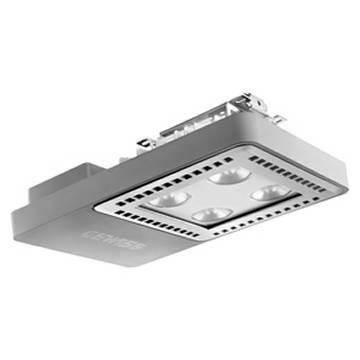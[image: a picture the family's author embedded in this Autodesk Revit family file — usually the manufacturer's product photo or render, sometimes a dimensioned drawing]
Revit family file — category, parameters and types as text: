
# Revit family: Lighting-Industrial-GEWISS-SMART[4]HE_HIGHBAYS-LED_1M
name_source: partatom
category: Apparecchi per illuminazione
units: mm (PartAtom-declared; Revit-internal decimal feet)

## family parameters
Basato su piano di lavoro = Sì
Condiviso = No
Numero OmniClass = 23.80.00.00
Punto di calcolo locali = Sì
Quota connettore circolare = Usa diametro
Sempre verticale = No
Sorgente d'illuminazione = No
Taglio con vuoti quando caricato = No
Tipo di parte = Normale
Titolo OmniClass = Electric Power and Lighting

## types (36) — shared parameters
Application = Internal
Body = PA6 "Halogen Free" loaded fibreglass
Carico apparente = 50 VA
Catalogue = LIGHTING
Classification: = -
Classificazione = Lighting
Color Rendering Index = CRI-80
Colour = Grey RAL 7035
Colour : = Grey RAL 7035
Commenti sul wattaggio = 50W
Context = Logistics and industrial manufacturing lighting
Control System = ON / OFF
Control System : = ON / OFF
DIN 18032-3 certification = With Bracket - Rope Kit + terminal&nbsp;(in approval)
Device with reduced surface temperature = Yes
Distanza tot_plafoniera = 74 mm  [stored 0.242782 ft]
Driver = Included
Driver Box = Built-in
Electrocod = 2444
Eletrical and lighting features = -
External screw = Stainless steel
Fixing = -
Gasket = anti-aging silicone
General information = -
Glow Wire Test : = 850 °C
IDF = caca2710-84d7-41a6-9312-c1c8a4914de0
IDT = 33be10311be341e0b261e3e80f29047b
IP degree = IP66
IPEA = -
Immagine tipo = GWL1071.jpg
Installationa and maintenance = -
Insulation class = I
LED Maintenance = Non-replaceable
Lampada = LED
Larghezza = 253 mm  [stored 0.830052 ft]
Lifetime = L90B10 (Tq+25°C) = 70.000 h - L90B10 (Tq+50°C) = 35.000 h
Locking Hook = -
Luminaire = LED Industrial ReflectorÂ
Lunghezza = 383 mm  [stored 1.25656 ft]
Materials = -
Maximum surface exposed to the wind : = 0,097 m²
Motore = <Per categoria>
Mouting and installation = Ceiling - Wallmounting - Suspension
Operating temperature : = -30°C ÷ +50 °C
Optic Maintenance = Non-replaceable
Optic and illuminating features = -
Overvoltage protection = DM 6kV / CM 6kV
Photobiological Risk Class = RG0
Plafoniera = <Per categoria>
Produttore = GEWISS S.p.A.
Prospetto di default = 1219 mm
Raggio led = 30 mm  [stored 0.0984252 ft]
Rated frequency (Hz) = 50/60 Hz
Shield type = Tempered glass Thickness 4mm
Shock resistance = IK08
Spessore plafoniera = 40 mm  [stored 0.131234 ft]
Standard Deviation Colour Matching = SDCM = 3
Standard- = EN 60598-1 ; EN 60598-2-1 ; EN 60598-2-24
Standards and approvals = -
Stocking temperature = -40 +70 °C
Supply voltage = 220 - 240 V
System power = 48W
Technical sheet = https://www.gewiss.com
Tilt- = With bracket accessory
Trasformatore = <Per categoria>
Type of light source = LED - Not replaceable
URL = https://www.gewiss.com
Unique digital code (Datamatrix) = Datamatrix
Version file RFA = 20.11
Vetro acceso = Lampada accesa
Voltaggio = 230 V
Warranty = 5 years
Weight (kg): = 3,5
Wiring = With GW connect watertight connector

## per-type parameters (varying)
| type | Colour temperature | Descrizione | Efficiency (lm/W) | Lumen output (lm) | Modello | Optic | Optic : | SEO | Unified Glare Rating |
| GWS4120AP857 - SMART4LB 1M ST.AL.ON/OFF 90° 57K | 5700K | SMART[4]LB 1M ST.AL.ON/OFF 90° 57K | 150 | 7200 | GWS4120AP857 | 90° | Metallic PC reflector and PMMA lenses |  | UGR - 25 |
| GWS4122AC830 - SMART4LB 1M C.PAS.ON/OFF ASI.30K | 3000K | SMART[4]LB 1M C.PAS.ON/OFF ASI.30K | 125 | 6000 | GWS4122AC830 | Asymmetrical | Metallic PC reflector and PMMA lenses | Low bay | - |
| GWS4120AQ857 - SMART4LB 1M ST.AL.ON/OFF ELL.57K | 5700K | SMART[4]LB 1M ST.AL.ON/OFF ELL.57K | 131 | 6300 | GWS4120AQ857 | Elliptical | Metallic PC reflector and PMMA lenses | Low bay | - |
| GWS4122AF830 - SMART4LB 1M C.PAS.ON/OFF 30° 30K | 3000K | SMART[4]LB 1M C.PAS.ON/OFF 30° 30K | 138 | 6600 | GWS4122AF830 | 30° | Metallic PC reflector and PMMA lenses |  | UGR - 22 |
| GWS4120AQ830 - SMART4LB 1M ST.AL.ON/OFF ELL.30K | 3000K | SMART[4]LB 1M ST.AL.ON/OFF ELL.30K | 125 | 6000 | GWS4120AQ830 | Elliptical | Metallic PC reflector and PMMA lenses | Low bay | - |
| GWS4122AQ840 - SMART4LB 1M C.PAS.ON/OFF ELL.40K | 4000K | SMART[4]LB 1M C.PAS.ON/OFF ELL.40K | 131 | 6300 | GWS4122AQ840 | Elliptical | Metallic PC reflector and PMMA lenses | Low bay | - |
| GWS4122AH857 - SMART4LB 1M C.PAS.ON/OFF 60° 57K | 5700K | SMART[4]LB 1M C.PAS.ON/OFF 60° 57K | 146 | 7000 | GWS4122AH857 | 60° | Metallic PC reflector and PMMA lenses |  | UGR - 22 |
| GWS4120AF830 - SMART4LB 1M ST.AL.ON/OFF 30° 30K | 3000K | SMART[4]LB 1M ST.AL.ON/OFF 30° 30K | 138 | 6600 | GWS4120AF830 | 30° | Metallic PC reflector and PMMA lenses |  | UGR - 22 |
| GWS4122AC857 - SMART4LB 1M C.PAS.ON/OFF ASI.57K | 5700K | SMART[4]LB 1M C.PAS.ON/OFF ASI.57K | 131 | 6300 | GWS4122AC857 | Asymmetrical | Metallic PC reflector and PMMA lenses | Low bay | - |
| GWS4120AH840 - SMART4LB 1M ST.AL.ON/OFF 60° 40K | 4000K | SMART[4]LB 1M ST.AL.ON/OFF 60° 40K | 146 | 7000 | GWS4120AH840 | 60° | Metallic PC reflector and PMMA lenses |  | UGR - 22 |
| GWS4122AP840 - SMART4LB 1M C.PAS.ON/OFF 90° 40K | 4000K | SMART[4]LB 1M C.PAS.ON/OFF 90° 40K | 150 | 7200 | GWS4122AP840 | 90° | Metallic PC reflector and PMMA lenses |  | UGR - 25 |
| GWS4120AH857 - SMART4LB 1M ST.AL.ON/OFF 60° 57K | 5700K | SMART[4]LB 1M ST.AL.ON/OFF 60° 57K | 146 | 7000 | GWS4120AH857 | 60° | Metallic PC reflector and PMMA lenses |  | UGR - 22 |
| GWS4122AP857 - SMART4LB 1M C.PAS.ON/OFF 90° 57K | 5700K | SMART[4]LB 1M C.PAS.ON/OFF 90° 57K | 150 | 7200 | GWS4122AP857 | 90° | Metallic PC reflector and PMMA lenses |  | UGR - 25 |
| GWS4120AA840 - SMART4LB 1M ST.AL.ON/OFF ARR.40K | 4000K | SMART[4]LB 1M ST.AL.ON/OFF ARR.40K | 148 | 7100 | GWS4120AA840 | Array | Metallized polycarbonate reflector |  | - |
| GWS4120AP830 - SMART4LB 1M ST.AL.ON/OFF 90° 30K | 3000K | SMART[4]LB 1M ST.AL.ON/OFF 90° 30K | 142 | 6800 | GWS4120AP830 | 90° | Metallic PC reflector and PMMA lenses |  | UGR - 25 |
| GWS4120AA830 - SMART4LB 1M ST.AL.ON/OFF ARR.30K | 3000K | SMART[4]LB 1M ST.AL.ON/OFF ARR.30K | 140 | 6700 | GWS4120AA830 | Array | Metallized polycarbonate reflector |  | - |
| GWS4122AA857 - SMART4LB 1M C.PAS.ON/OFF ARR.57K | 5700K | SMART[4]LB 1M C.PAS.ON/OFF ARR.57K | 148 | 7100 | GWS4122AA857 | Array | Metallized polycarbonate reflector |  | - |
| GWS4122AC840 - SMART4LB 1M C.PAS.ON/OFF ASI.40K | 4000K | SMART[4]LB 1M C.PAS.ON/OFF ASI.40K | 131 | 6300 | GWS4122AC840 | Asymmetrical | Metallic PC reflector and PMMA lenses | Low bay | - |
| GWS4120AH830 - SMART4LB 1M ST.AL.ON/OFF 60° 30K | 3000K | SMART[4]LB 1M ST.AL.ON/OFF 60° 30K | 140 | 6700 | GWS4120AH830 | 60° | Metallic PC reflector and PMMA lenses |  | UGR - 22 |
| GWS4120AA857 - SMART4LB 1M ST.AL.ON/OFF ARR.57K | 5700K | SMART[4]LB 1M ST.AL.ON/OFF ARR.57K | 148 | 7100 | GWS4120AA857 | Array | Metallized polycarbonate reflector |  | - |
| GWS4122AQ857 - SMART4LB 1M C.PAS.ON/OFF ELL.57K | 5700K | SMART[4]LB 1M C.PAS.ON/OFF ELL.57K | 131 | 6300 | GWS4122AQ857 | Elliptical | Metallic PC reflector and PMMA lenses | Low bay | - |
| GWS4122AA830 - SMART4LB 1M C.PAS.ON/OFF ARR.30K | 3000K | SMART[4]LB 1M C.PAS.ON/OFF ARR.30K | 140 | 6700 | GWS4122AA830 | Array | Metallized polycarbonate reflector |  | - |
| GWS4120AP840 - SMART4LB 1M ST.AL.ON/OFF 90° 40K | 4000K | SMART[4]LB 1M ST.AL.ON/OFF 90° 40K | 150 | 7200 | GWS4120AP840 | 90° | Metallic PC reflector and PMMA lenses |  | UGR - 25 |
| GWS4122AQ830 - SMART4LB 1M C.PAS.ON/OFF ELL.30K | 3000K | SMART[4]LB 1M C.PAS.ON/OFF ELL.30K | 125 | 6000 | GWS4122AQ830 | Elliptical | Metallic PC reflector and PMMA lenses | Low bay | - |
| GWS4120AC830 - SMART4LB 1M ST.AL.ON/OFF ASI.30K | 3000K | SMART[4]LB 1M ST.AL.ON/OFF ASI.30K | 125 | 6000 | GWS4120AC830 | Asymmetrical | Metallic PC reflector and PMMA lenses | Low bay | - |
| GWS4120AC857 - SMART4LB 1M ST.AL.ON/OFF ASI.57K | 5700K | SMART[4]LB 1M ST.AL.ON/OFF ASI.57K | 131 | 6300 | GWS4120AC857 | Asymmetrical | Metallic PC reflector and PMMA lenses | Low bay | - |
| GWS4122AF840 - SMART4LB 1M C.PAS.ON/OFF 30° 40K | 4000K | SMART[4]LB 1M C.PAS.ON/OFF 30° 40K | 146 | 7000 | GWS4122AF840 | 30° | Metallic PC reflector and PMMA lenses |  | UGR - 22 |
| GWS4122AP830 - SMART4LB 1M C.PAS.ON/OFF 90° 30K | 3000K | SMART[4]LB 1M C.PAS.ON/OFF 90° 30K | 142 | 6800 | GWS4122AP830 | 90° | Metallic PC reflector and PMMA lenses |  | UGR - 25 |
| GWS4122AF857 - SMART4LB 1M C.PAS.ON/OFF 30° 57K | 5700K | SMART[4]LB 1M C.PAS.ON/OFF 30° 57K | 146 | 7000 | GWS4122AF857 | 30° | Metallic PC reflector and PMMA lenses |  | UGR - 22 |
| GWS4120AQ840 - SMART4LB 1M ST.AL.ON/OFF ELL.40K | 4000K | SMART[4]LB 1M ST.AL.ON/OFF ELL.40K | 131 | 6300 | GWS4120AQ840 | Elliptical | Metallic PC reflector and PMMA lenses | Low bay | - |
| GWS4122AH840 - SMART4LB 1M C.PAS.ON/OFF 60° 40K | 4000K | SMART[4]LB 1M C.PAS.ON/OFF 60° 40K | 146 | 7000 | GWS4122AH840 | 60° | Metallic PC reflector and PMMA lenses |  | UGR - 22 |
| GWS4122AA840 - SMART4LB 1M C.PAS.ON/OFF ARR.40K | 4000K | SMART[4]LB 1M C.PAS.ON/OFF ARR.40K | 148 | 7100 | GWS4122AA840 | Array | Metallized polycarbonate reflector |  | - |
| GWS4120AF857 - SMART4LB 1M ST.AL.ON/OFF 30° 57K | 5700K | SMART[4]LB 1M ST.AL.ON/OFF 30° 57K | 146 | 7000 | GWS4120AF857 | 30° | Metallic PC reflector and PMMA lenses |  | UGR - 22 |
| GWS4122AH830 - SMART4LB 1M C.PAS.ON/OFF 60° 30K | 3000K | SMART[4]LB 1M C.PAS.ON/OFF 60° 30K | 140 | 6700 | GWS4122AH830 | 60° | Metallic PC reflector and PMMA lenses |  | UGR - 22 |
| GWS4120AF840 - SMART4LB 1M ST.AL.ON/OFF 30° 40K | 4000K | SMART[4]LB 1M ST.AL.ON/OFF 30° 40K | 146 | 7000 | GWS4120AF840 | 30° | Metallic PC reflector and PMMA lenses |  | UGR - 22 |
| GWS4120AC840 - SMART4LB 1M ST.AL.ON/OFF ASI.40K | 4000K | SMART[4]LB 1M ST.AL.ON/OFF ASI.40K | 131 | 6300 | GWS4120AC840 | Asymmetrical | Metallic PC reflector and PMMA lenses | Low bay | - |

note: [stored X ft] marks values corroborated as IEEE doubles in the binary element streams (Revit-internal decimal feet)

## geometry (parser evidence)
native form markers: Blend x4
no freeform markers — native parametric forms only
